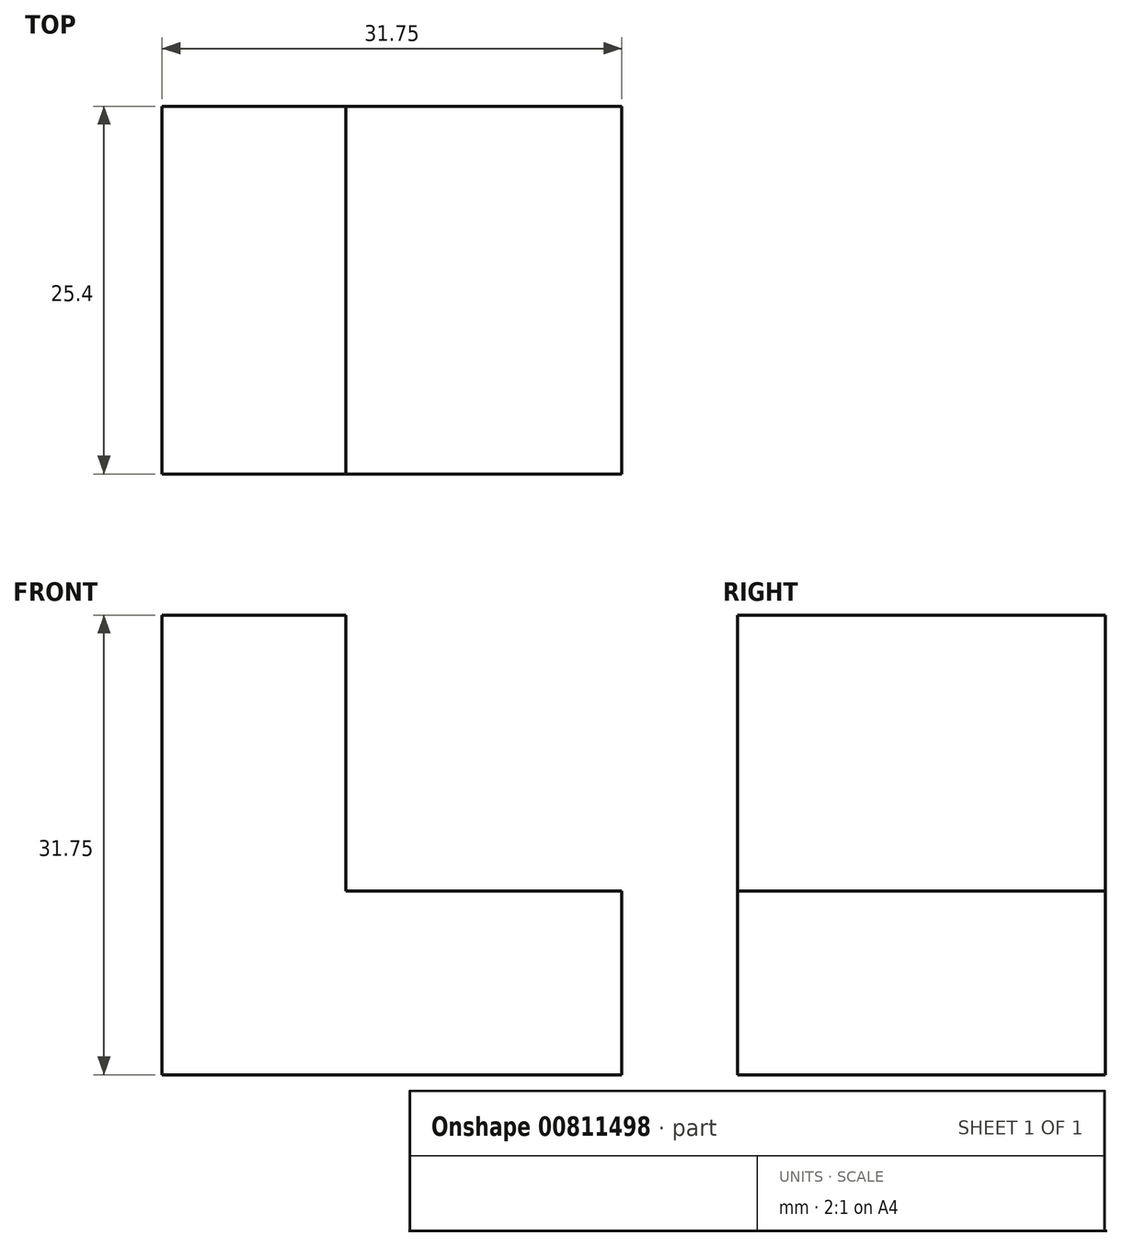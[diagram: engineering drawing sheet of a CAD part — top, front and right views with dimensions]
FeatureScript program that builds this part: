
annotation { "Feature Type Name" : "Feature", "Feature Type Description" : "" }
export const myFeature = defineFeature(function(context is Context, id is Id, definition is map)
    precondition{}
    {
        {
            var Q0;
            Q0=qCreatedBy(makeId("Front.planeOp"),FACE);
            var sketch = newSketch(context, id + "F0", { "sketchPlane" : qUnion([Q0])});
            skLineSegment(sketch, "E0", {"start": v(0, 0) * mm, "end": v(0, 31.75) * mm});
            skLineSegment(sketch, "E1", {"start": v(0, 31.75) * mm, "end": v(12.7, 31.75) * mm});
            skLineSegment(sketch, "E2", {"start": v(12.7, 31.75) * mm, "end": v(12.7, 12.7) * mm});
            skLineSegment(sketch, "E3", {"start": v(12.7, 12.7) * mm, "end": v(31.75, 12.7) * mm});
            skLineSegment(sketch, "E4", {"start": v(31.75, 12.7) * mm, "end": v(31.75, 0) * mm});
            skLineSegment(sketch, "E5", {"start": v(31.75, 0) * mm, "end": v(0, 0) * mm});
            skSolve(sketch);
        }
        {
            var Q0;
            Q0=makeQuery(id+"F0.imprint","IMPRINT",FACE,{"disambiguationData":[TD([[makeQuery(id+"F0.imprint","IMPRINT",EDGE,{"derivedFrom":sQuery(id+"F0.wireOp",EDGE,"E0")}),-1.0]])]});
            extrude(context, id + "F1", {"entities" : qUnion([Q0]), "depth" : 25.4 * mm, "offsetDistance" : 25.4 * mm});
        }
    });
